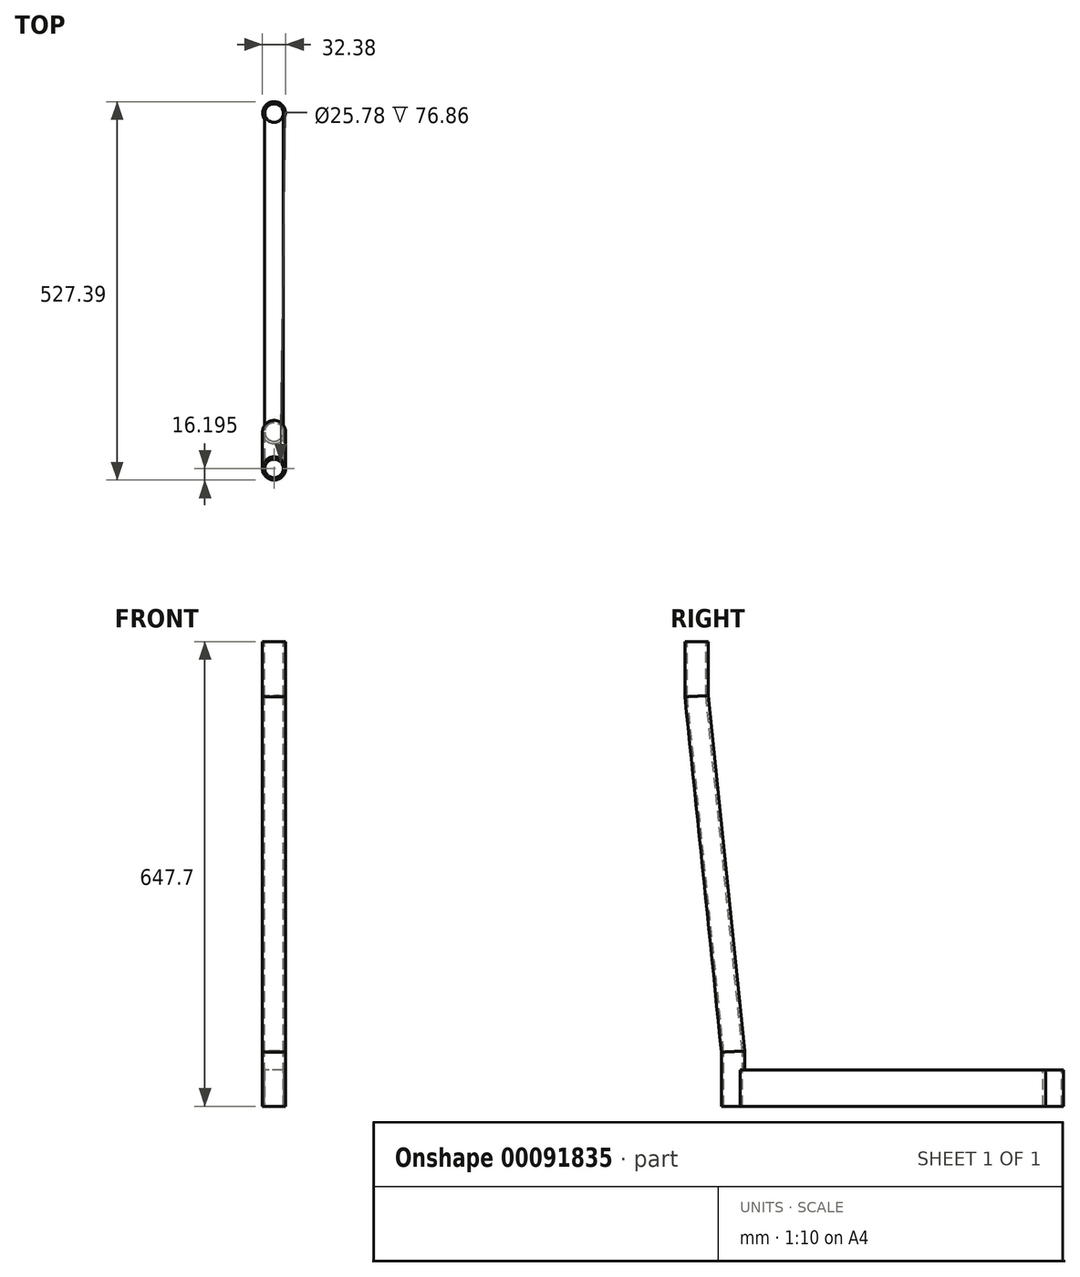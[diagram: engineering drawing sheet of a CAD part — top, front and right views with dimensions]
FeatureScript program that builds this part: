
annotation { "Feature Type Name" : "Feature", "Feature Type Description" : "" }
export const myFeature = defineFeature(function(context is Context, id is Id, definition is map)
    precondition{}
    {
        {
            var Q0;
            Q0=qCreatedBy(makeId("Top.planeOp"),FACE);
            var sketch = newSketch(context, id + "F0", { "sketchPlane" : qUnion([Q0])});
            skCircle(sketch, "E0", {"center": v(0, 0) * mm, "radius": 15.88 * mm});
            skLineSegment(sketch, "E1", {"start": v(-12.9, -9.27) * mm, "end": v(-12.9, -434.72) * mm});
            skLineSegment(sketch, "E2", {"start": v(12.9, -9.27) * mm, "end": v(12.9, -434.72) * mm});
            skCircle(sketch, "E3", {"center": v(0, -444.52) * mm, "radius": 16.2 * mm});
            skLineSegment(sketch, "E4", {"start": v(-12.9, -222) * mm, "end": v(12.9, -222) * mm});
            skCircle(sketch, "E5", {"center": v(0, -444.52) * mm, "radius": 12.9 * mm});
            skSolve(sketch);
        }
        {
            var Q0;
            {var subQ0=sQuery(id+"F0.wireOp",EDGE,"E0");var subQ1=makeQuery(id+"F0.imprint","INTERSECT",VERTEX,{"derivedFrom":[subQ0,sQuery(id+"F0.wireOp",EDGE,"E1")]});Q0=makeQuery(id+"F0.imprint","IMPRINT",FACE,{"disambiguationData":[TD([[makeQuery(id+"F0.imprint","IMPRINT",EDGE,{"disambiguationData":[TD([[subQ1,-1.0]])],"derivedFrom":subQ0}),1.0]])]});}
            var Q1;
            {var subQ5=sQuery(id+"F0.wireOp",EDGE,"E4");Q1=makeQuery(id+"F0.imprint","IMPRINT",FACE,{"disambiguationData":[TD([[makeQuery(id+"F0.imprint","IMPRINT",EDGE,{"derivedFrom":subQ5}),1.0]])]});}
            var Q2;
            {var subQ3=sQuery(id+"F0.wireOp",EDGE,"E4");Q2=makeQuery(id+"F0.imprint","IMPRINT",FACE,{"disambiguationData":[TD([[makeQuery(id+"F0.imprint","IMPRINT",EDGE,{"derivedFrom":subQ3}),-1.0]])]});}
            extrude(context, id + "F1", {"entities" : qUnion([Q0, Q1, Q2]), "depth" : 50.8 * mm});
        }
        {
            var Q0;
            Q0=makeQuery(id+"F1.opExtrude","CAP_FACE",FACE,{"disambiguationData":[OSD([sQuery(id+"F0.wireOp",EDGE,"E0"),sQuery(id+"F0.wireOp",EDGE,"E1"),sQuery(id+"F0.wireOp",EDGE,"E2"),sQuery(id+"F0.wireOp",EDGE,"E3")])],"isStart":false});
            var sketch = newSketch(context, id + "F2", { "sketchPlane" : qUnion([Q0])});
            skCircle(sketch, "E6", {"center": v(0, 0) * mm, "radius": 12.9 * mm});
            skSolve(sketch);
        }
        {
            var Q0;
            Q0=makeQuery(id+"F2.imprint","IMPRINT",FACE,{"disambiguationData":[TD([[makeQuery(id+"F2.imprint","IMPRINT",EDGE,{"derivedFrom":sQuery(id+"F2.wireOp",EDGE,"E6")}),1.0]])]});
            var Q1;
            Q1=makeQuery(id+"F1.opExtrude","CAP_FACE",FACE,{"disambiguationData":[OSD([sQuery(id+"F0.wireOp",EDGE,"E0"),sQuery(id+"F0.wireOp",EDGE,"E1"),sQuery(id+"F0.wireOp",EDGE,"E2"),sQuery(id+"F0.wireOp",EDGE,"E3")])],"isStart":true});
            extrude(context, id + "F3", {"entities" : qUnion([Q0]), "operationType" : NewBodyOperationType.REMOVE, "endBound" : BoundingType.UP_TO_SURFACE, "oppositeDirection" : true, "endBoundEntityFace" : qUnion([Q1]), "depth" : 25.4 * mm});
        }
        {
            var Q0;
            Q0=qCreatedBy(makeId("Right.planeOp"),FACE);
            var sketch = newSketch(context, id + "F4", { "sketchPlane" : qUnion([Q0])});
            skPoint(sketch, "E7.0", {"position": v(-444.52, 0) * mm});
            skLineSegment(sketch, "E8", {"start": v(-444.52, 0) * mm, "end": v(-444.52, 647.7) * mm, "construction": true});
            skLineSegment(sketch, "E9", {"start": v(-444.52, 647.7) * mm, "end": v(-495.32, 647.7) * mm, "construction": true});
            skLineSegment(sketch, "E10", {"start": v(-495.32, 647.7) * mm, "end": v(-495.32, 571.5) * mm});
            skLineSegment(sketch, "E11", {"start": v(-444.52, 0) * mm, "end": v(-444.52, 76.2) * mm});
            skLineSegment(sketch, "E12", {"start": v(-444.52, 76.2) * mm, "end": v(-495.32, 571.5) * mm});
            skSolve(sketch);
        }
        {
            var Q0;
            {var subQ0=sQuery(id+"F0.wireOp",EDGE,"E3");var subQ1=makeQuery(id+"F0.imprint","INTERSECT",VERTEX,{"derivedFrom":[sQuery(id+"F0.wireOp",EDGE,"E1"),subQ0]});Q0=makeQuery(id+"F0.imprint","IMPRINT",FACE,{"disambiguationData":[TD([[makeQuery(id+"F0.imprint","IMPRINT",EDGE,{"disambiguationData":[TD([[subQ1,1.0]])],"derivedFrom":subQ0}),1.0]])]});}
            var Q1;
            Q1=sQuery(id+"F4.wireOp",EDGE,"E11");
            var Q2;
            Q2=sQuery(id+"F4.wireOp",EDGE,"E12");
            var Q3;
            Q3=sQuery(id+"F4.wireOp",EDGE,"E10");
            sweep(context, id + "F5", {"operationType" : NewBodyOperationType.ADD, "profiles" : qUnion([Q0]), "path" : qUnion([Q1, Q2, Q3])});
        }
    });
